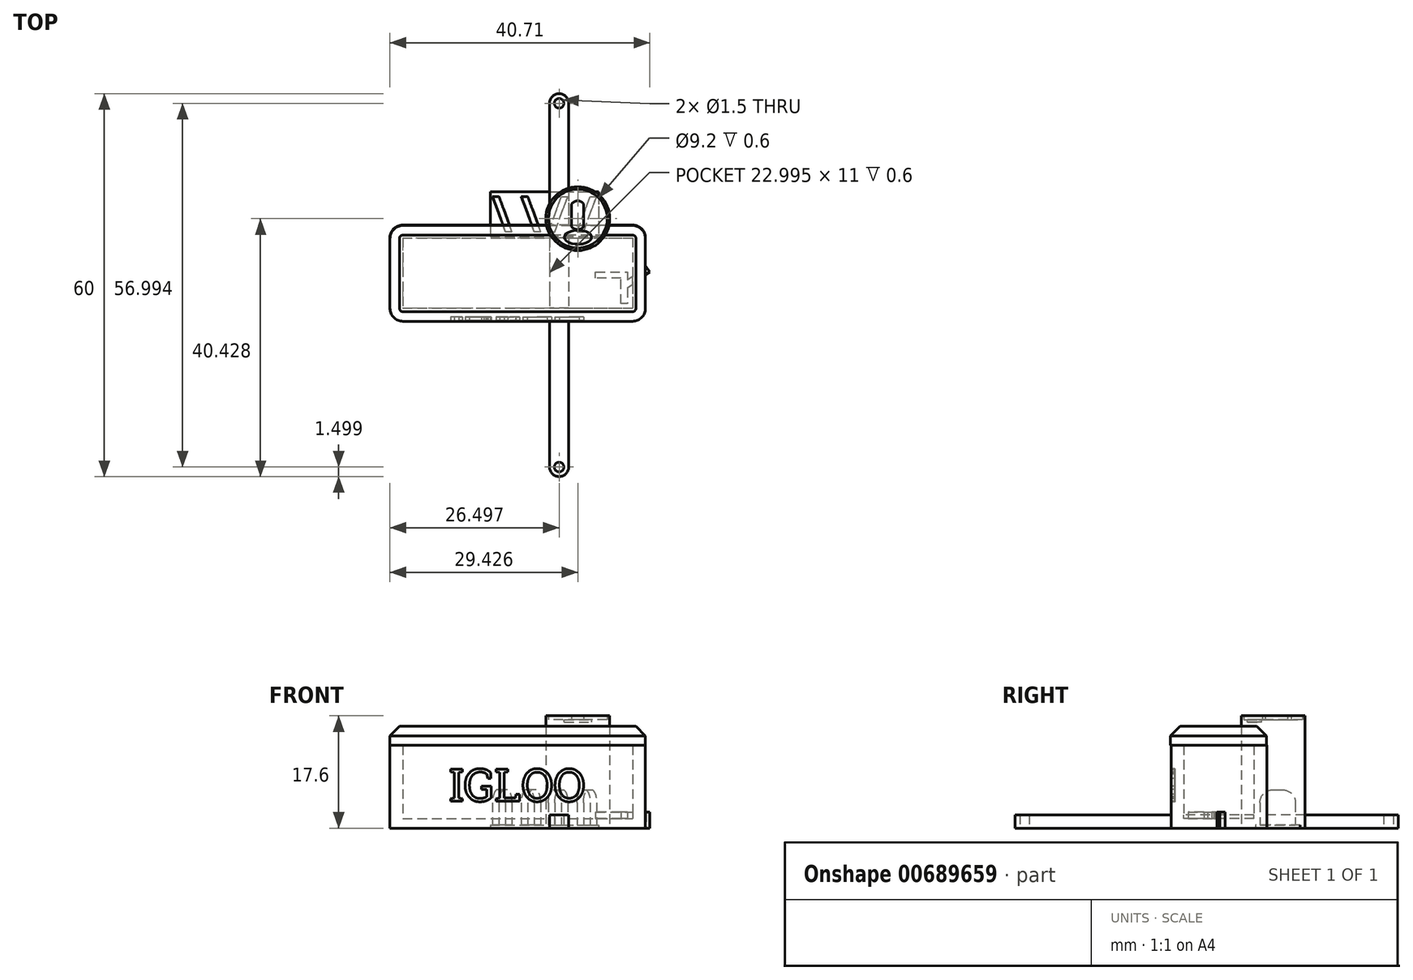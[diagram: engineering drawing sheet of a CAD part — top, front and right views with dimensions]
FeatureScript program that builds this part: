
annotation { "Feature Type Name" : "Feature", "Feature Type Description" : "" }
export const myFeature = defineFeature(function(context is Context, id is Id, definition is map)
    precondition{}
    {
        {
            var Q0;
            Q0=qCreatedBy(makeId("Top.planeOp"),FACE);
            var sketch = newSketch(context, id + "F0", { "sketchPlane" : qUnion([Q0])});
            skLineSegment(sketch, "E0.bottom", {"start": v(-33.42, 28.37) * mm, "end": v(-16.42, 28.37) * mm});
            skLineSegment(sketch, "E0.top", {"start": v(-33.42, 21.37) * mm, "end": v(-16.42, 21.37) * mm});
            skLineSegment(sketch, "E0.left", {"start": v(-33.42, 28.37) * mm, "end": v(-33.42, 21.37) * mm});
            skLineSegment(sketch, "E0.right", {"start": v(-16.42, 28.37) * mm, "end": v(-16.42, 21.37) * mm});
            skPoint(sketch, "E1", {"position": v(-24.92, 28.37) * mm});
            skPoint(sketch, "E2", {"position": v(-24.92, 21.37) * mm});
            skPoint(sketch, "E3", {"position": v(-23.56, 21.37) * mm});
            skLineSegment(sketch, "E4", {"start": v(-23.31, 22.05) * mm, "end": v(-21.29, 27.6) * mm});
            skPoint(sketch, "E5", {"position": v(-20.06, 21.37) * mm});
            skPoint(sketch, "E6", {"position": v(-17.51, 28.37) * mm});
            skLineSegment(sketch, "E7", {"start": v(-19.81, 22.05) * mm, "end": v(-17.79, 27.6) * mm});
            skPoint(sketch, "E8", {"position": v(-16.51, 28.37) * mm});
            skPoint(sketch, "E9", {"position": v(-19.06, 21.37) * mm});
            skLineSegment(sketch, "E10", {"start": v(-18.81, 22.05) * mm, "end": v(-16.79, 27.6) * mm});
            skPoint(sketch, "E11", {"position": v(-22.01, 28.37) * mm});
            skPoint(sketch, "E12", {"position": v(-24.56, 21.37) * mm});
            skLineSegment(sketch, "E13", {"start": v(-24.31, 22.05) * mm, "end": v(-22.29, 27.6) * mm});
            skPoint(sketch, "E14", {"position": v(-17.79, 27.6) * mm});
            skPoint(sketch, "E14.positionSnap0", {"position": v(-17.79, 24.87) * mm});
            skPoint(sketch, "E15", {"position": v(-16.79, 27.6) * mm});
            skPoint(sketch, "E16", {"position": v(-21.29, 27.6) * mm});
            skPoint(sketch, "E17", {"position": v(-22.29, 27.6) * mm});
            skPoint(sketch, "E18", {"position": v(-18.81, 22.05) * mm});
            skPoint(sketch, "E19", {"position": v(-19.81, 22.05) * mm});
            skPoint(sketch, "E20", {"position": v(-23.31, 22.05) * mm});
            skPoint(sketch, "E21", {"position": v(-24.31, 22.05) * mm});
            skPoint(sketch, "E22.orphan", {"position": v(-21.01, 28.37) * mm});
            skLineSegment(sketch, "E23", {"start": v(-22.29, 27.6) * mm, "end": v(-21.29, 27.6) * mm});
            skLineSegment(sketch, "E24", {"start": v(-24.31, 22.05) * mm, "end": v(-23.31, 22.05) * mm});
            skLineSegment(sketch, "E25", {"start": v(-19.81, 22.05) * mm, "end": v(-18.81, 22.05) * mm});
            skLineSegment(sketch, "E26", {"start": v(-17.79, 27.6) * mm, "end": v(-16.79, 27.6) * mm});
            skLineSegment(sketch, "E27.MirrorCS", {"start": v(-26.53, 22.05) * mm, "end": v(-28.55, 27.6) * mm});
            skLineSegment(sketch, "E28.MirrorCS", {"start": v(-25.53, 22.05) * mm, "end": v(-27.55, 27.6) * mm});
            skLineSegment(sketch, "E29.MirrorCS", {"start": v(-27.55, 27.6) * mm, "end": v(-28.55, 27.6) * mm});
            skLineSegment(sketch, "E30.MirrorCS", {"start": v(-25.53, 22.05) * mm, "end": v(-26.53, 22.05) * mm});
            skLineSegment(sketch, "E31.MirrorCS", {"start": v(-30.03, 22.05) * mm, "end": v(-31.03, 22.05) * mm});
            skLineSegment(sketch, "E32.MirrorCS", {"start": v(-30.03, 22.05) * mm, "end": v(-32.05, 27.6) * mm});
            skLineSegment(sketch, "E33.MirrorCS", {"start": v(-31.03, 22.05) * mm, "end": v(-33.05, 27.6) * mm});
            skLineSegment(sketch, "E34.MirrorCS", {"start": v(-32.05, 27.6) * mm, "end": v(-33.05, 27.6) * mm});
            skSolve(sketch);
        }
        {
            var Q0;
            Q0=makeQuery(id+"F0.imprint","IMPRINT",FACE,{"disambiguationData":[TD([[makeQuery(id+"F0.imprint","IMPRINT",EDGE,{"derivedFrom":sQuery(id+"F0.wireOp",EDGE,"E0.bottom")}),-1.0]])]});
            extrude(context, id + "F1", {"entities" : qUnion([Q0]), "depth" : .5 * mm, "offsetDistance" : 25.4 * mm});
        }
        {
            var Q0;
            Q0=makeQuery(id+"F0.imprint","IMPRINT",FACE,{"disambiguationData":[TD([[makeQuery(id+"F0.imprint","IMPRINT",EDGE,{"derivedFrom":sQuery(id+"F0.wireOp",EDGE,"E31.MirrorCS")}),-1.0]])]});
            var Q1;
            Q1=makeQuery(id+"F0.imprint","IMPRINT",FACE,{"disambiguationData":[TD([[makeQuery(id+"F0.imprint","IMPRINT",EDGE,{"derivedFrom":sQuery(id+"F0.wireOp",EDGE,"E27.MirrorCS")}),-1.0]])]});
            var Q2;
            Q2=makeQuery(id+"F0.imprint","IMPRINT",FACE,{"disambiguationData":[TD([[makeQuery(id+"F0.imprint","IMPRINT",EDGE,{"derivedFrom":sQuery(id+"F0.wireOp",EDGE,"E4")}),1.0]])]});
            var Q3;
            Q3=makeQuery(id+"F0.imprint","IMPRINT",FACE,{"disambiguationData":[TD([[makeQuery(id+"F0.imprint","IMPRINT",EDGE,{"derivedFrom":sQuery(id+"F0.wireOp",EDGE,"E7")}),-1.0]])]});
            extrude(context, id + "F2", {"entities" : qUnion([Q0, Q1, Q2, Q3]), "operationType" : NewBodyOperationType.ADD, "depth" : 6 * mm, "offsetDistance" : 25.4 * mm});
        }
        {
            var Q0;
            Q0=makeQuery(id+"F2.opExtrude","CAP_EDGE",EDGE,{"disambiguationData":[OSD([sQuery(id+"F0.wireOp",EDGE,"E31.MirrorCS")])],"isStart":false});
            var Q1;
            Q1=makeQuery(id+"F2.opExtrude","CAP_EDGE",EDGE,{"disambiguationData":[OSD([sQuery(id+"F0.wireOp",EDGE,"E34.MirrorCS")])],"isStart":false});
            var Q2;
            Q2=makeQuery(id+"F2.opExtrude","CAP_EDGE",EDGE,{"disambiguationData":[OSD([sQuery(id+"F0.wireOp",EDGE,"E30.MirrorCS")])],"isStart":false});
            var Q3;
            Q3=makeQuery(id+"F2.opExtrude","CAP_EDGE",EDGE,{"disambiguationData":[OSD([sQuery(id+"F0.wireOp",EDGE,"E29.MirrorCS")])],"isStart":false});
            var Q4;
            Q4=makeQuery(id+"F2.opExtrude","CAP_EDGE",EDGE,{"disambiguationData":[OSD([sQuery(id+"F0.wireOp",EDGE,"E24")])],"isStart":false});
            var Q5;
            Q5=makeQuery(id+"F2.opExtrude","CAP_EDGE",EDGE,{"disambiguationData":[OSD([sQuery(id+"F0.wireOp",EDGE,"E23")])],"isStart":false});
            var Q6;
            Q6=makeQuery(id+"F2.opExtrude","CAP_EDGE",EDGE,{"disambiguationData":[OSD([sQuery(id+"F0.wireOp",EDGE,"E26")])],"isStart":false});
            var Q7;
            Q7=makeQuery(id+"F2.opExtrude","CAP_EDGE",EDGE,{"disambiguationData":[OSD([sQuery(id+"F0.wireOp",EDGE,"E25")])],"isStart":false});
            fillet(context, id + "F3", {"entities" : qUnion([Q0, Q1, Q2, Q3, Q4, Q5, Q6, Q7]), "radius" : 2 * mm, "tangentPropagation" : true, "allowEdgeOverflow" : false});
        }
        {
            var Q0;
            Q0=qCreatedBy(makeId("Top.planeOp"),FACE);
            var sketch = newSketch(context, id + "F4", { "sketchPlane" : qUnion([Q0])});
            skLineSegment(sketch, "E35", {"start": v(-12.93, 10.8) * mm, "end": v(-12.93, 14.8) * mm});
            skLineSegment(sketch, "E36", {"start": v(-12.93, 14.8) * mm, "end": v(-16.93, 14.8) * mm});
            skLineSegment(sketch, "E37", {"start": v(-16.93, 14.8) * mm, "end": v(-16.93, 15.8) * mm});
            skLineSegment(sketch, "E38", {"start": v(-16.93, 15.8) * mm, "end": v(-11.93, 15.8) * mm});
            skLineSegment(sketch, "E39", {"start": v(-11.93, 15.8) * mm, "end": v(-11.93, 10.8) * mm});
            skLineSegment(sketch, "E40", {"start": v(-11.93, 10.8) * mm, "end": v(-12.93, 10.8) * mm});
            skPoint(sketch, "E41.start.orphan", {"position": v(-11.93, 13.3) * mm});
            skPoint(sketch, "E42", {"position": v(-8.43, 15.8) * mm});
            skLineSegment(sketch, "E43", {"start": v(-11.93, 13.3) * mm, "end": v(-8.43, 15.8) * mm});
            skLineSegment(sketch, "E44", {"start": v(-8.43, 15.8) * mm, "end": v(-9.01, 16.61) * mm});
            skLineSegment(sketch, "E45", {"start": v(-9.01, 16.61) * mm, "end": v(-11.93, 14.53) * mm});
            skSolve(sketch);
        }
        {
            var Q0;
            Q0=makeQuery(id+"F4.imprint","IMPRINT",FACE,{"disambiguationData":[TD([[makeQuery(id+"F4.imprint","IMPRINT",EDGE,{"derivedFrom":sQuery(id+"F4.wireOp",EDGE,"E35")}),-1.0]])]});
            var Q1;
            {var subQ0=sQuery(id+"F4.wireOp",EDGE,"E43");Q1=makeQuery(id+"F4.imprint","IMPRINT",FACE,{"disambiguationData":[TD([[makeQuery(id+"F4.imprint","IMPRINT",EDGE,{"derivedFrom":subQ0}),1.0]])]});}
            extrude(context, id + "F5", {"entities" : qUnion([Q0, Q1]), "depth" : 2.5 * mm, "offsetDistance" : 25.4 * mm});
        }
        {
            var Q0;
            Q0=qCreatedBy(makeId("Top.planeOp"),FACE);
            var sketch = newSketch(context, id + "F6", { "sketchPlane" : qUnion([Q0])});
            skLineSegment(sketch, "E46.bottom", {"start": v(-24.14, 42.2) * mm, "end": v(-21.14, 42.2) * mm});
            skLineSegment(sketch, "E46.top", {"start": v(-24.14, -14.8) * mm, "end": v(-21.14, -14.8) * mm});
            skLineSegment(sketch, "E46.left", {"start": v(-24.14, 42.2) * mm, "end": v(-24.14, -14.8) * mm});
            skLineSegment(sketch, "E46.right", {"start": v(-21.14, 42.2) * mm, "end": v(-21.14, -14.8) * mm});
            skArc(sketch, "E47", {"start": v(-21.14, 42.2) * mm, "mid": v(-22.64, 43.7) * mm, "end": v(-24.14, 42.2) * mm});
            skPoint(sketch, "E48.orphan", {"position": v(-22.64, 43.7) * mm});
            skCircle(sketch, "E49", {"center": v(-22.64, 42.2) * mm, "radius": 0.75 * mm});
            skPoint(sketch, "E50.start.orphan", {"position": v(-21.14, 13.7) * mm});
            skPoint(sketch, "E51.positionSnap0", {"position": v(-22.64, -14.8) * mm});
            skArc(sketch, "E52", {"start": v(-24.14, -14.8) * mm, "mid": v(-22.64, -16.3) * mm, "end": v(-21.14, -14.8) * mm});
            skPoint(sketch, "E53", {"position": v(-22.64, -16.3) * mm});
            skCircle(sketch, "E54", {"center": v(-22.64, -14.8) * mm, "radius": 0.75 * mm});
            skSolve(sketch);
        }
        {
            var Q0;
            {var subQ4=sQuery(id+"F6.wireOp",EDGE,"E46.left");Q0=makeQuery(id+"F6.imprint","IMPRINT",FACE,{"disambiguationData":[TD([[makeQuery(id+"F6.imprint","IMPRINT",EDGE,{"derivedFrom":subQ4}),1.0]])]});}
            var Q1;
            {var subQ4=sQuery(id+"F6.wireOp",EDGE,"E47");Q1=makeQuery(id+"F6.imprint","IMPRINT",FACE,{"disambiguationData":[TD([[makeQuery(id+"F6.imprint","IMPRINT",EDGE,{"derivedFrom":subQ4}),1.0]])]});}
            var Q2;
            {var subQ3=sQuery(id+"F6.wireOp",EDGE,"E52");Q2=makeQuery(id+"F6.imprint","IMPRINT",FACE,{"disambiguationData":[TD([[makeQuery(id+"F6.imprint","IMPRINT",EDGE,{"derivedFrom":subQ3}),1.0]])]});}
            extrude(context, id + "F7", {"entities" : qUnion([Q0, Q1, Q2]), "depth" : 2.1 * mm, "offsetDistance" : 25.4 * mm});
        }
        {
            var Q0;
            Q0=qCreatedBy(makeId("Top.planeOp"),FACE);
            var sketch = newSketch(context, id + "F8", { "sketchPlane" : qUnion([Q0])});
            skLineSegment(sketch, "E55.bottom", {"start": v(-49.14, 23.12) * mm, "end": v(-9.14, 23.12) * mm});
            skLineSegment(sketch, "E55.top", {"start": v(-49.14, 8.12) * mm, "end": v(-9.14, 8.12) * mm});
            skLineSegment(sketch, "E55.left", {"start": v(-49.14, 23.12) * mm, "end": v(-49.14, 8.12) * mm});
            skLineSegment(sketch, "E55.right", {"start": v(-9.14, 23.12) * mm, "end": v(-9.14, 8.12) * mm});
            skPoint(sketch, "E56", {"position": v(-9.14, 10.12) * mm});
            skPoint(sketch, "E57", {"position": v(-11.14, 10.12) * mm});
            skPoint(sketch, "E58", {"position": v(-47.14, 23.12) * mm});
            skPoint(sketch, "E59", {"position": v(-47.14, 21.12) * mm});
            skLineSegment(sketch, "E60.bottom", {"start": v(-47.14, 21.12) * mm, "end": v(-11.14, 21.12) * mm});
            skLineSegment(sketch, "E60.top", {"start": v(-47.14, 10.12) * mm, "end": v(-11.14, 10.12) * mm});
            skLineSegment(sketch, "E60.left", {"start": v(-47.14, 21.12) * mm, "end": v(-47.14, 10.12) * mm});
            skLineSegment(sketch, "E60.right", {"start": v(-11.14, 21.12) * mm, "end": v(-11.14, 10.12) * mm});
            skSolve(sketch);
        }
        {
            var Q0;
            Q0=makeQuery(id+"F8.imprint","IMPRINT",FACE,{"disambiguationData":[TD([[makeQuery(id+"F8.imprint","IMPRINT",EDGE,{"derivedFrom":sQuery(id+"F8.wireOp",EDGE,"E55.bottom")}),-1.0]])]});
            extrude(context, id + "F9", {"entities" : qUnion([Q0]), "depth" : 13 * mm, "offsetDistance" : 25.4 * mm});
        }
        {
            var Q0;
            Q0=makeQuery(id+"F8.imprint","IMPRINT",FACE,{"disambiguationData":[TD([[makeQuery(id+"F8.imprint","IMPRINT",EDGE,{"derivedFrom":sQuery(id+"F8.wireOp",EDGE,"E60.bottom")}),-1.0]])]});
            extrude(context, id + "F10", {"entities" : qUnion([Q0]), "operationType" : NewBodyOperationType.ADD, "depth" : 1.5 * mm, "offsetDistance" : 25.4 * mm});
        }
        {
            var Q0;
            Q0=makeQuery(id+"F9.opExtrude","SWEPT_EDGE",EDGE,{"disambiguationData":[OSD([sQuery(id+"F8.wireOp",EDGE,"E55.top"),sQuery(id+"F8.wireOp",EDGE,"E55.right")])]});
            var Q1;
            Q1=makeQuery(id+"F9.opExtrude","SWEPT_EDGE",EDGE,{"disambiguationData":[OSD([sQuery(id+"F8.wireOp",EDGE,"E55.bottom"),sQuery(id+"F8.wireOp",EDGE,"E55.right")])]});
            var Q2;
            Q2=makeQuery(id+"F9.opExtrude","SWEPT_EDGE",EDGE,{"disambiguationData":[OSD([sQuery(id+"F8.wireOp",EDGE,"E55.top"),sQuery(id+"F8.wireOp",EDGE,"E55.left")])]});
            var Q3;
            Q3=makeQuery(id+"F9.opExtrude","SWEPT_EDGE",EDGE,{"disambiguationData":[OSD([sQuery(id+"F8.wireOp",EDGE,"E55.bottom"),sQuery(id+"F8.wireOp",EDGE,"E55.left")])]});
            fillet(context, id + "F11", {"entities" : qUnion([Q0, Q1, Q2, Q3]), "tangentPropagation" : true, "radius" : 2 * mm, "defaultsChanged" : true, "vertexSettings" : [], "allowEdgeOverflow" : false});
        }
        {
            var Q0;
            Q0=qCreatedBy(makeId("Top.planeOp"),FACE);
            var sketch = newSketch(context, id + "F12", { "sketchPlane" : qUnion([Q0])});
            skLineSegment(sketch, "E61.bottom", {"start": v(7.59, 21.55) * mm, "end": v(47.59, 21.55) * mm});
            skLineSegment(sketch, "E61.top", {"start": v(7.59, 6.55) * mm, "end": v(47.59, 6.55) * mm});
            skLineSegment(sketch, "E61.left", {"start": v(7.59, 21.55) * mm, "end": v(7.59, 6.55) * mm});
            skLineSegment(sketch, "E61.right", {"start": v(47.59, 21.55) * mm, "end": v(47.59, 6.55) * mm});
            skPoint(sketch, "E62", {"position": v(47.59, 7.75) * mm});
            skPoint(sketch, "E63", {"position": v(46.39, 7.75) * mm});
            skPoint(sketch, "E64", {"position": v(8.79, 21.55) * mm});
            skPoint(sketch, "E65", {"position": v(8.79, 20.35) * mm});
            skLineSegment(sketch, "E66.bottom", {"start": v(8.79, 20.35) * mm, "end": v(46.39, 20.35) * mm});
            skLineSegment(sketch, "E66.top", {"start": v(8.79, 7.75) * mm, "end": v(46.39, 7.75) * mm});
            skLineSegment(sketch, "E66.left", {"start": v(8.79, 20.35) * mm, "end": v(8.79, 7.75) * mm});
            skLineSegment(sketch, "E66.right", {"start": v(46.39, 20.35) * mm, "end": v(46.39, 7.75) * mm});
            skSolve(sketch);
        }
        {
            var Q0;
            Q0=makeQuery(id+"F12.imprint","IMPRINT",FACE,{"disambiguationData":[TD([[makeQuery(id+"F12.imprint","IMPRINT",EDGE,{"derivedFrom":sQuery(id+"F12.wireOp",EDGE,"E66.bottom")}),-1.0]])]});
            var Q1;
            Q1=makeQuery(id+"F12.imprint","IMPRINT",FACE,{"disambiguationData":[TD([[makeQuery(id+"F12.imprint","IMPRINT",EDGE,{"derivedFrom":sQuery(id+"F12.wireOp",EDGE,"E61.bottom")}),-1.0]])]});
            extrude(context, id + "F13", {"entities" : qUnion([Q0, Q1]), "depth" : 3 * mm, "offsetDistance" : 25.4 * mm});
        }
        {
            var Q0;
            Q0=makeQuery(id+"F13.opExtrude","SWEPT_EDGE",EDGE,{"disambiguationData":[OSD([sQuery(id+"F12.wireOp",EDGE,"E61.top"),sQuery(id+"F12.wireOp",EDGE,"E61.right")])]});
            var Q1;
            Q1=makeQuery(id+"F13.opExtrude","SWEPT_EDGE",EDGE,{"disambiguationData":[OSD([sQuery(id+"F12.wireOp",EDGE,"E61.bottom"),sQuery(id+"F12.wireOp",EDGE,"E61.right")])]});
            var Q2;
            Q2=makeQuery(id+"F13.opExtrude","SWEPT_EDGE",EDGE,{"disambiguationData":[OSD([sQuery(id+"F12.wireOp",EDGE,"E61.top"),sQuery(id+"F12.wireOp",EDGE,"E61.left")])]});
            var Q3;
            Q3=makeQuery(id+"F13.opExtrude","SWEPT_EDGE",EDGE,{"disambiguationData":[OSD([sQuery(id+"F12.wireOp",EDGE,"E61.bottom"),sQuery(id+"F12.wireOp",EDGE,"E61.left")])]});
            fillet(context, id + "F14", {"entities" : qUnion([Q0, Q1, Q2, Q3]), "tangentPropagation" : true, "radius" : 2 * mm, "defaultsChanged" : true, "vertexSettings" : [], "allowEdgeOverflow" : false});
        }
        {
            var Q0;
            Q0=makeQuery(id+"F13.opExtrude","CAP_EDGE",EDGE,{"disambiguationData":[OSD([sQuery(id+"F12.wireOp",EDGE,"E61.top")])],"isStart":false});
            chamfer(context, id + "F15", {"entities" : qUnion([Q0]), "width" : 1.5 * mm, "tangentPropagation" : true});
        }
        {
            var Q0;
            Q0=makeQuery(id+"F9.opExtrude","SWEPT_FACE",FACE,{"disambiguationData":[OSD([sQuery(id+"F8.wireOp",EDGE,"E55.top")])]});
            var sketch = newSketch(context, id + "F16", { "sketchPlane" : qUnion([Q0])});
            skPoint(sketch, "E67", {"position": v(-29.14, 13) * mm});
            skText(sketch, "E68", { "text": "IGLOO", "fontName": "RobotoSlab-Regular.ttf"});
            const initialGuessF16  = {"E68": [-0.03985, 0.0042, 1, 0, 0.00512]};
            skSetInitialGuess(sketch, initialGuessF16);
            skSolve(sketch);
        }
        {
            var Q0;
            Q0=makeQuery(id+"F16.imprint","IMPRINT",FACE,{"disambiguationData":[TD([[makeQuery(id+"F16.imprint","IMPRINT",EDGE,{"derivedFrom":sQuery(id+"F16.wireOp",EDGE,"E68.sketch_text.stroke-0")}),-1.0]])]});
            var Q1;
            Q1=makeQuery(id+"F16.imprint","IMPRINT",FACE,{"disambiguationData":[TD([[makeQuery(id+"F16.imprint","IMPRINT",EDGE,{"derivedFrom":sQuery(id+"F16.wireOp",EDGE,"E68.sketch_text.stroke-12")}),-1.0]])]});
            var Q2;
            Q2=makeQuery(id+"F16.imprint","IMPRINT",FACE,{"disambiguationData":[TD([[makeQuery(id+"F16.imprint","IMPRINT",EDGE,{"derivedFrom":sQuery(id+"F16.wireOp",EDGE,"E68.sketch_text.stroke-38")}),-1.0]])]});
            var Q3;
            Q3=makeQuery(id+"F16.imprint","IMPRINT",FACE,{"disambiguationData":[TD([[makeQuery(id+"F16.imprint","IMPRINT",EDGE,{"derivedFrom":sQuery(id+"F16.wireOp",EDGE,"E68.sketch_text.stroke-54")}),-1.0]])]});
            var Q4;
            Q4=makeQuery(id+"F16.imprint","IMPRINT",FACE,{"disambiguationData":[TD([[makeQuery(id+"F16.imprint","IMPRINT",EDGE,{"derivedFrom":sQuery(id+"F16.wireOp",EDGE,"E68.sketch_text.stroke-74")}),-1.0]])]});
            extrude(context, id + "F17", {"entities" : qUnion([Q0, Q1, Q2, Q3, Q4]), "operationType" : NewBodyOperationType.REMOVE, "oppositeDirection" : true, "depth" : .6 * mm, "offsetDistance" : 25.4 * mm});
        }
        {
            var Q0;
            Q0=makeQuery(id+"F13.opExtrude","SWEPT_BODY",BODY,{"disambiguationData":[OSD([sQuery(id+"F12.wireOp",EDGE,"E61.bottom"),sQuery(id+"F12.wireOp",EDGE,"E61.top"),sQuery(id+"F12.wireOp",EDGE,"E61.left"),sQuery(id+"F12.wireOp",EDGE,"E61.right")])]});
            transform(context, id + "F18", {"entities" : qUnion([Q0]), "transformType" : TransformType.TRANSLATION_3D, "dx" : -56.72 * mm, "dy" : 1.5 * mm, "dz" : 12.98 * mm, "makeCopy" : false});
        }
        {
            var Q0;
            Q0=qCreatedBy(makeId("Top.planeOp"),FACE);
            var sketch = newSketch(context, id + "F19", { "sketchPlane" : qUnion([Q0])});
            skCircle(sketch, "E69", {"center": v(-19.71, 24.14) * mm, "radius": 5 * mm});
            skSolve(sketch);
        }
        {
            var Q0;
            Q0=makeQuery(id+"F19.imprint","IMPRINT",FACE,{"disambiguationData":[TD([[makeQuery(id+"F19.imprint","IMPRINT",EDGE,{"derivedFrom":sQuery(id+"F19.wireOp",EDGE,"E69")}),1.0]])]});
            extrude(context, id + "F20", {"entities" : qUnion([Q0]), "depth" : 17 * mm, "offsetDistance" : 25.4 * mm});
        }
        {
            var Q0;
            Q0=makeQuery(id+"F20.opExtrude","CAP_FACE",FACE,{"disambiguationData":[OSD([sQuery(id+"F19.wireOp",EDGE,"E69")])],"isStart":false});
            var sketch = newSketch(context, id + "F21", { "sketchPlane" : qUnion([Q0])});
            skCircle(sketch, "E70", {"center": v(-19.71, 24.14) * mm, "radius": 4.6 * mm});
            skLineSegment(sketch, "E71.bottom", {"start": v(-20.7, 22.9) * mm, "end": v(-18.78, 22.9) * mm});
            skLineSegment(sketch, "E71.left", {"start": v(-20.7, 22.9) * mm, "end": v(-20.7, 26.37) * mm});
            skLineSegment(sketch, "E71.right", {"start": v(-18.78, 22.9) * mm, "end": v(-18.78, 26.37) * mm});
            skArc(sketch, "E72", {"start": v(-20.7, 22.9) * mm, "mid": v(-19.74, 22.42) * mm, "end": v(-18.78, 22.9) * mm});
            skArc(sketch, "E73", {"start": v(-18.78, 26.37) * mm, "mid": v(-19.74, 26.93) * mm, "end": v(-20.7, 26.37) * mm});
            skArc(sketch, "E74", {"start": v(-20.7, 26.37) * mm, "mid": v(-19.74, 25.84) * mm, "end": v(-18.78, 26.37) * mm});
            skLineSegment(sketch, "E75", {"start": v(-19.74, 25.84) * mm, "end": v(-18.78, 25.84) * mm});
            skLineSegment(sketch, "E76", {"start": v(-19.74, 25.84) * mm, "end": v(-20.7, 25.84) * mm});
            skLineSegment(sketch, "E77", {"start": v(-20.7, 25.4) * mm, "end": v(-18.78, 25.4) * mm});
            skEllipse(sketch, "E78", {"center": v(-19.68, 21.21) * mm, "majorRadius": 2.14 * mm, "minorRadius": 1.1 * mm, "majorAxis": v(-1, 0)});
            skSolve(sketch);
        }
        {
            var Q0;
            Q0=makeQuery(id+"F21.imprint","IMPRINT",FACE,{"disambiguationData":[TD([[makeQuery(id+"F21.imprint","IMPRINT",EDGE,{"derivedFrom":sQuery(id+"F21.wireOp",EDGE,"E70")}),-1.0]])]});
            var Q1;
            {var subQ0=sQuery(id+"F21.wireOp",EDGE,"E75");Q1=makeQuery(id+"F21.imprint","IMPRINT",FACE,{"disambiguationData":[TD([[makeQuery(id+"F21.imprint","IMPRINT",EDGE,{"derivedFrom":subQ0}),-1.0]])]});}
            var Q2;
            {var subQ3=sQuery(id+"F21.wireOp",EDGE,"E75");Q2=makeQuery(id+"F21.imprint","IMPRINT",FACE,{"disambiguationData":[TD([[makeQuery(id+"F21.imprint","IMPRINT",EDGE,{"derivedFrom":subQ3}),1.0]])]});}
            var Q3;
            {var subQ3=sQuery(id+"F21.wireOp",EDGE,"E76");Q3=makeQuery(id+"F21.imprint","IMPRINT",FACE,{"disambiguationData":[TD([[makeQuery(id+"F21.imprint","IMPRINT",EDGE,{"derivedFrom":subQ3}),-1.0]])]});}
            var Q4;
            Q4=makeQuery(id+"F21.imprint","IMPRINT",FACE,{"disambiguationData":[TD([[makeQuery(id+"F21.imprint","IMPRINT",EDGE,{"derivedFrom":sQuery(id+"F21.wireOp",EDGE,"E71.bottom")}),-1.0]])]});
            var Q5;
            {var subQ0=sQuery(id+"F21.wireOp",EDGE,"E71.bottom");Q5=makeQuery(id+"F21.imprint","IMPRINT",FACE,{"disambiguationData":[TD([[makeQuery(id+"F21.imprint","IMPRINT",EDGE,{"derivedFrom":subQ0}),1.0]])]});}
            var Q6;
            {var subQ0=sQuery(id+"F21.wireOp",EDGE,"E73");Q6=makeQuery(id+"F21.imprint","IMPRINT",FACE,{"disambiguationData":[TD([[makeQuery(id+"F21.imprint","IMPRINT",EDGE,{"derivedFrom":subQ0}),1.0]])]});}
            extrude(context, id + "F22", {"entities" : qUnion([Q0, Q1, Q2, Q3, Q4, Q5, Q6]), "operationType" : NewBodyOperationType.ADD, "depth" : .6 * mm, "offsetDistance" : 25.4 * mm});
        }
        {
            var Q0;
            Q0=makeQuery(id+"F21.imprint","IMPRINT",FACE,{"disambiguationData":[TD([[makeQuery(id+"F21.imprint","IMPRINT",EDGE,{"derivedFrom":sQuery(id+"F21.wireOp",EDGE,"E78")}),1.0]])]});
            extrude(context, id + "F23", {"entities" : qUnion([Q0]), "operationType" : NewBodyOperationType.REMOVE, "oppositeDirection" : true, "depth" : .4 * mm, "offsetDistance" : 25.4 * mm});
        }
    });
